# Revit family: Урна «Парк М. Горького» Арт 10386.jpg
name_source: partatom
category: Антураж
revit_build: Autodesk Revit 2018 (Build: 20180423_1000(x64)
units: mm (PartAtom-declared; Revit-internal decimal feet)

## family parameters
Всегда вертикально = Да
Источник визуального образа = Геометрия семейства
На основе рабочей плоскости = Нет
Общий = Нет
При загрузке вырезать с полостями = Нет
Точка расчета площади = Нет

## types (2) — shared parameters
URL = https://hobbyka.ru
Артикул товара = Арт. 10386
Высота = 800 мм
Группа модели = Уличные урны
Диаметр = 450 мм
Длина = 450 мм
Изготовитель = ООО «Хоббика»
Изображение типоразмера = Урна «Парк М. Горького» На одной опоре, без пепельницы Арт 10386.jpg
Материал изделия = Сталь, дерево
Цвет отделки = Дерево
Цвет урны = Сталь
Ширина = 450 мм

## per-type parameters (varying)
| type | Одна опора | Описание | Стандарт |
| Урна «Парк М. Горького». Версия На одной опоре, без пепельницы | Да | Урна «Парк М. Горького». Версия: На одной опоре, без пепельницы | Нет |
| Урна «Парк М. Горького». Версия Стандарт, без пепельницы | Нет | Урна «Парк М. Горького». Версия: Стандарт, без пепельницы | Да |
